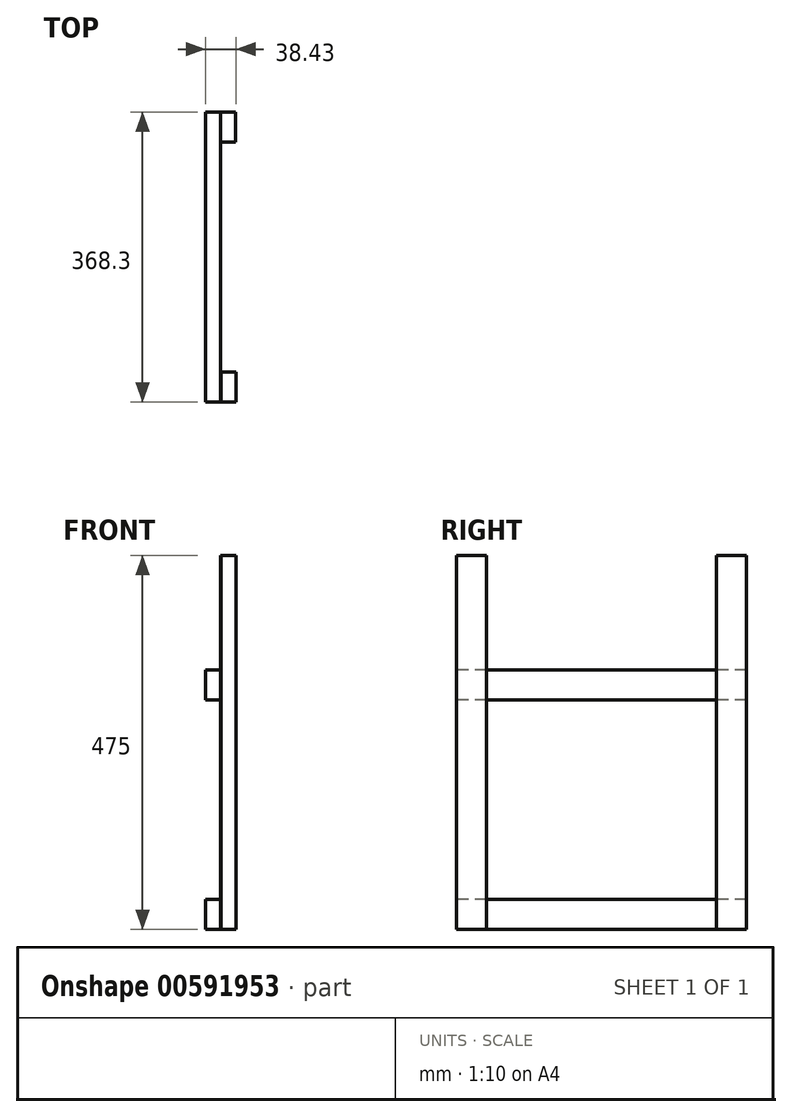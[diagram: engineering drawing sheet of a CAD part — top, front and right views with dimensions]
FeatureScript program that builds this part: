
annotation { "Feature Type Name" : "Feature", "Feature Type Description" : "" }
export const myFeature = defineFeature(function(context is Context, id is Id, definition is map)
    precondition{}
    {
        {
            var Q0;
            Q0=qCreatedBy(makeId("Top.planeOp"),FACE);
            var sketch = newSketch(context, id + "F0", { "sketchPlane" : qUnion([Q0])});
            skLineSegment(sketch, "E0.bottom", {"start": v(-80.77, 62.5) * mm, "end": v(-61.72, 62.5) * mm});
            skLineSegment(sketch, "E0.top", {"start": v(-80.77, 24.4) * mm, "end": v(-61.72, 24.4) * mm});
            skLineSegment(sketch, "E0.left", {"start": v(-80.77, 62.5) * mm, "end": v(-80.77, 24.4) * mm});
            skLineSegment(sketch, "E0.right", {"start": v(-61.72, 62.5) * mm, "end": v(-61.72, 24.4) * mm});
            skSolve(sketch);
        }
        {
            var Q0;
            Q0=makeQuery(id+"F0.imprint","IMPRINT",FACE,{"disambiguationData":[TD([[makeQuery(id+"F0.imprint","IMPRINT",EDGE,{"derivedFrom":sQuery(id+"F0.wireOp",EDGE,"E0.bottom")}),-1.0]])]});
            extrude(context, id + "F1", {"entities" : qUnion([Q0]), "depth" : 475 * mm, "offsetDistance" : 25.4 * mm});
        }
        {
            var Q0;
            Q0=qCreatedBy(makeId("Top.planeOp"),FACE);
            var sketch = newSketch(context, id + "F2", { "sketchPlane" : qUnion([Q0])});
            skLineSegment(sketch, "E1.bottom", {"start": v(-80.44, -267.7) * mm, "end": v(-61.4, -267.7) * mm});
            skLineSegment(sketch, "E1.top", {"start": v(-80.44, -305.8) * mm, "end": v(-61.4, -305.8) * mm});
            skLineSegment(sketch, "E1.left", {"start": v(-80.44, -267.7) * mm, "end": v(-80.44, -305.8) * mm});
            skLineSegment(sketch, "E1.right", {"start": v(-61.4, -267.7) * mm, "end": v(-61.4, -305.8) * mm});
            skSolve(sketch);
        }
        {
            var Q0;
            Q0=makeQuery(id+"F2.imprint","IMPRINT",FACE,{"disambiguationData":[TD([[makeQuery(id+"F2.imprint","IMPRINT",EDGE,{"derivedFrom":sQuery(id+"F2.wireOp",EDGE,"E1.bottom")}),-1.0]])]});
            extrude(context, id + "F3", {"entities" : qUnion([Q0]), "depth" : 475 * mm, "offsetDistance" : 25.4 * mm});
        }
        {
            var Q0;
            Q0=makeQuery(id+"F1.opExtrude","SWEPT_FACE",FACE,{"disambiguationData":[OSD([sQuery(id+"F0.wireOp",EDGE,"E0.left")])]});
            var sketch = newSketch(context, id + "F4", { "sketchPlane" : qUnion([Q0])});
            skLineSegment(sketch, "E2.bottom", {"start": v(-62.5, 0) * mm, "end": v(305.8, 0) * mm});
            skLineSegment(sketch, "E2.top", {"start": v(-62.5, 38.1) * mm, "end": v(305.8, 38.1) * mm});
            skLineSegment(sketch, "E2.left", {"start": v(-62.5, 0) * mm, "end": v(-62.5, 38.1) * mm});
            skLineSegment(sketch, "E2.right", {"start": v(305.8, 0) * mm, "end": v(305.8, 38.1) * mm});
            skSolve(sketch);
        }
        {
            var Q0;
            Q0 = qSketchRegion(id + "F4", true);
            extrude(context, id + "F5", {"entities" : qUnion([Q0]), "depth" : 19.05 * mm, "offsetDistance" : 25.4 * mm});
        }
        {
            var Q0;
            Q0=makeQuery(id+"F1.opExtrude","SWEPT_FACE",FACE,{"disambiguationData":[OSD([sQuery(id+"F0.wireOp",EDGE,"E0.left")])]});
            var sketch = newSketch(context, id + "F6", { "sketchPlane" : qUnion([Q0])});
            skLineSegment(sketch, "E3.bottom", {"start": v(-62.5, 291.85) * mm, "end": v(305.8, 291.85) * mm});
            skLineSegment(sketch, "E3.top", {"start": v(-62.5, 329.95) * mm, "end": v(305.8, 329.95) * mm});
            skLineSegment(sketch, "E3.left", {"start": v(-62.5, 291.85) * mm, "end": v(-62.5, 329.95) * mm});
            skLineSegment(sketch, "E3.right", {"start": v(305.8, 291.85) * mm, "end": v(305.8, 329.95) * mm});
            skSolve(sketch);
        }
        {
            var Q0;
            Q0 = qSketchRegion(id + "F6", true);
            extrude(context, id + "F7", {"entities" : qUnion([Q0]), "depth" : 19.05 * mm, "offsetDistance" : 25.4 * mm});
        }
    });
